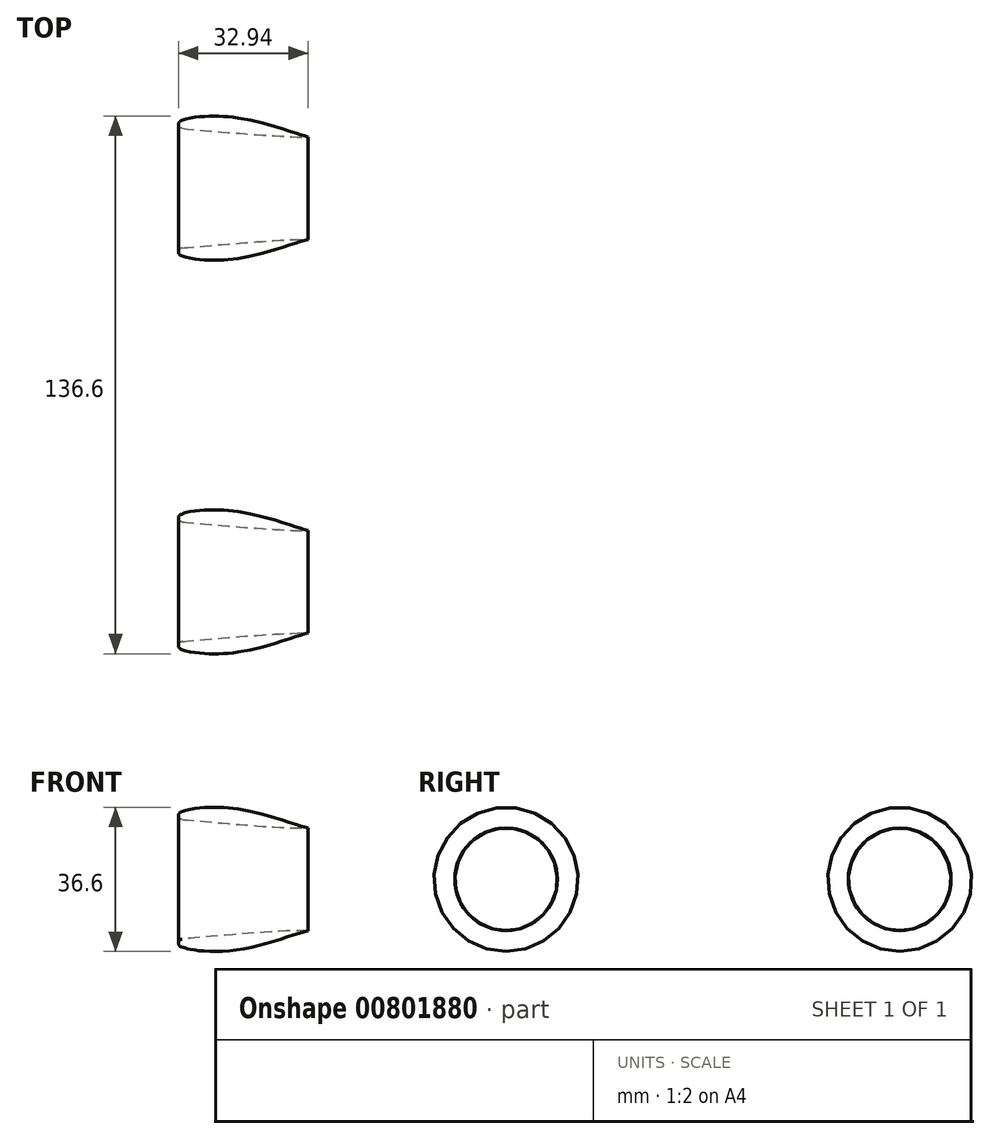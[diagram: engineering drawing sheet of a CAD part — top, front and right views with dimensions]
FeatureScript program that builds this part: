
annotation { "Feature Type Name" : "Feature", "Feature Type Description" : "" }
export const myFeature = defineFeature(function(context is Context, id is Id, definition is map)
    precondition{}
    {
        {
            var Q0;
            Q0=qCreatedBy(makeId("Front.planeOp"),FACE);
            var sketch = newSketch(context, id + "F0", { "sketchPlane" : qUnion([Q0])});
            skLineSegment(sketch, "E0", {"start": v(0, 0) * mm, "end": v(-99.04, 0) * mm, "construction": true});
            skPoint(sketch, "E1", {"position": v(-90.27, 34.91) * mm});
            skPoint(sketch, "E2", {"position": v(-50.85, 34.91) * mm});
            skPoint(sketch, "E3", {"position": v(-50.85, 8.8) * mm});
            skPoint(sketch, "E4.third.point", {"position": v(-82.79, 11.97) * mm});
            skArc(sketch, "E5", {"start": v(-83.1, 12.91) * mm, "mid": v(-83.78, 11.87) * mm, "end": v(-82.92, 10.98) * mm});
            skFitSpline(sketch, "E6", {"points": [v(-50.85, 8.8) * mm, v(-67.9, 13.52) * mm, v(-81.03, 13.53) * mm, v(-83.1, 12.91) * mm], "startDerivative": vector(-22.24, 5.67) * mm, "endDerivative": vector(-9.62, -3.28) * mm});
            skFitSpline(sketch, "E7", {"points": [v(-50.85, 8.8) * mm, v(-80.69, 10.77) * mm, v(-82.92, 10.98) * mm], "startDerivative": vector(-23.35, -0.8) * mm, "endDerivative": vector(-6.4, 0.87) * mm});
            skLineSegment(sketch, "E8", {"start": v(0, -4.23) * mm, "end": v(-99.04, -4.23) * mm, "construction": true});
            skSolve(sketch);
        }
        {
            var Q0;
            Q0 = qSketchRegion(id + "F0", true);
            var Q1;
            Q1=sQuery(id+"F0.wireOp",EDGE,"E8");
            revolve(context, id + "F1", {"surfaceOperationType" : NewSurfaceOperationType.NEW, "entities" : qUnion([Q0]), "axis" : qUnion([Q1]), "revolveType" : RevolveType.FULL});
        }
        {
            var Q0;
            Q0=makeQuery(id+"F1.opRevolve","SWEPT_BODY",BODY,{"disambiguationData":[OSD([sQuery(id+"F0.wireOp",EDGE,"E5"),sQuery(id+"F0.wireOp",EDGE,"E6"),sQuery(id+"F0.wireOp",EDGE,"E7")])]});
            transform(context, id + "F2", {"entities" : qUnion([Q0]), "transformType" : TransformType.TRANSLATION_3D, "dx" : 0 * mm, "dy" : -100 * mm, "dz" : 0 * mm, "makeCopy" : true});
        }
    });
